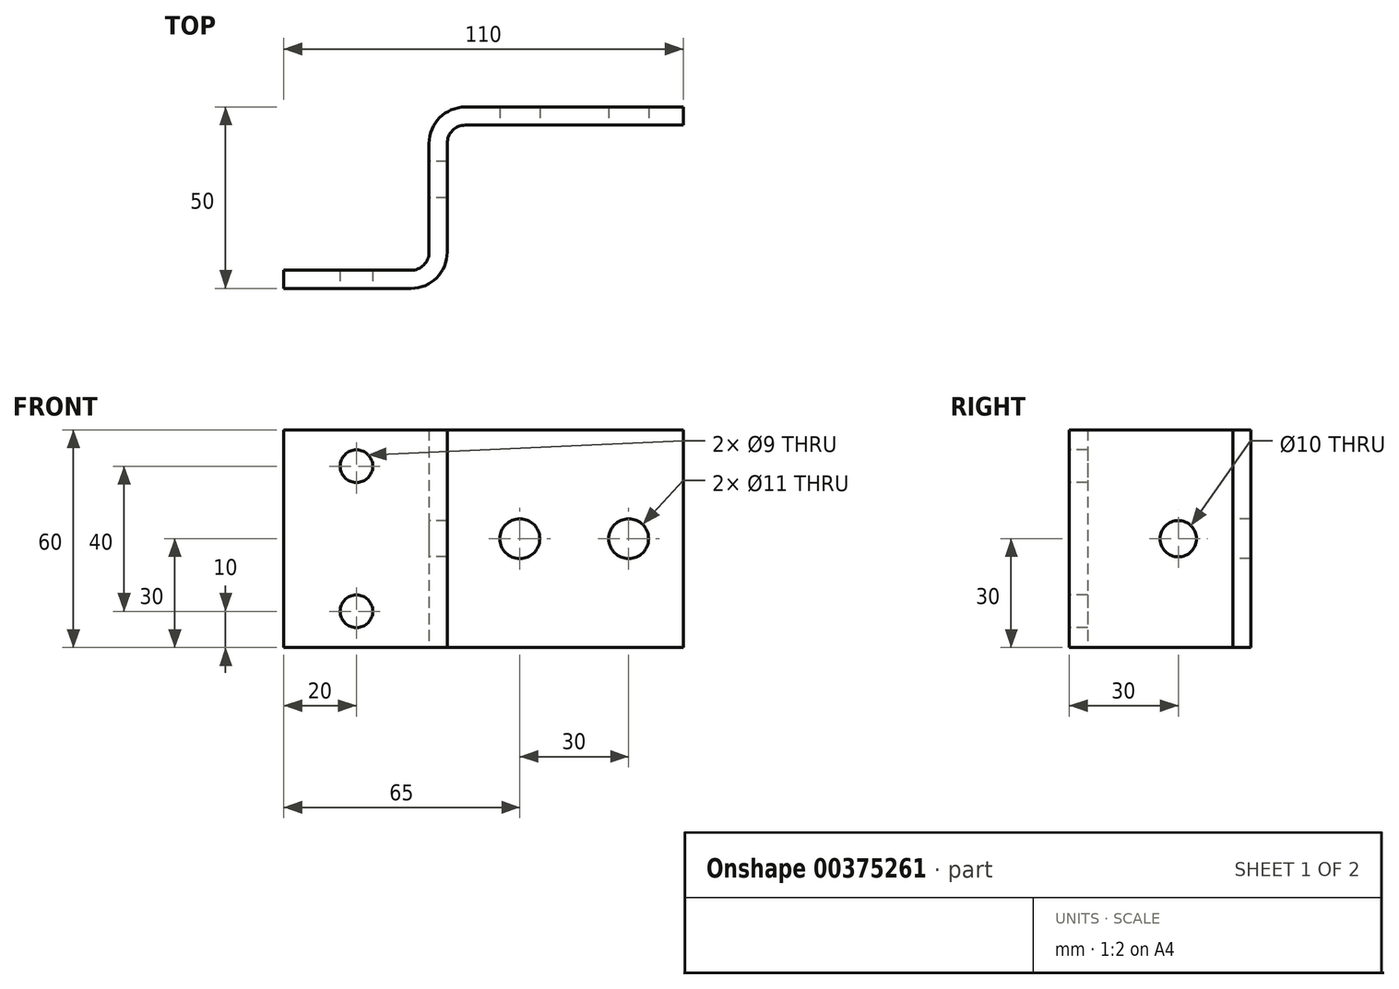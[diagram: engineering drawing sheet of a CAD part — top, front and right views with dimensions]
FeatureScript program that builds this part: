
annotation { "Feature Type Name" : "Feature", "Feature Type Description" : "" }
export const myFeature = defineFeature(function(context is Context, id is Id, definition is map)
    precondition{}
    {
        {
            var Q0;
            Q0=qCreatedBy(makeId("Top.planeOp"),FACE);
            var sketch = newSketch(context, id + "F0", { "sketchPlane" : qUnion([Q0])});
            skLineSegment(sketch, "E0", {"start": v(0, 0) * mm, "end": v(0, 5) * mm});
            skLineSegment(sketch, "E1", {"start": v(0, 5) * mm, "end": v(35, 5) * mm});
            skLineSegment(sketch, "E2", {"start": v(35, 0) * mm, "end": v(0, 0) * mm});
            skLineSegment(sketch, "E3", {"start": v(40, 10) * mm, "end": v(40, 40) * mm});
            skLineSegment(sketch, "E4", {"start": v(50, 50) * mm, "end": v(110, 50) * mm});
            skLineSegment(sketch, "E5", {"start": v(110, 50) * mm, "end": v(110, 45) * mm});
            skLineSegment(sketch, "E6", {"start": v(110, 45) * mm, "end": v(50, 45) * mm});
            skLineSegment(sketch, "E7", {"start": v(45, 40) * mm, "end": v(45, 10) * mm});
            skPoint(sketch, "E8.visualSharp", {"position": v(45, 0) * mm});
            skArc(sketch, "E8.filletArc", {"start": v(35, 0) * mm, "mid": v(42.07, 2.93) * mm, "end": v(45, 10) * mm});
            skPoint(sketch, "E9.orphan", {"position": v(40, 0) * mm});
            skPoint(sketch, "E10.visualSharp", {"position": v(40, 5) * mm});
            skArc(sketch, "E10.filletArc", {"start": v(35, 5) * mm, "mid": v(38.54, 6.46) * mm, "end": v(40, 10) * mm});
            skPoint(sketch, "E11.orphan", {"position": v(40, 45) * mm});
            skPoint(sketch, "E12.visualSharp", {"position": v(45, 45) * mm});
            skArc(sketch, "E12.filletArc", {"start": v(50, 45) * mm, "mid": v(46.46, 43.54) * mm, "end": v(45, 40) * mm});
            skPoint(sketch, "E13.visualSharp", {"position": v(40, 50) * mm});
            skArc(sketch, "E13.filletArc", {"start": v(50, 50) * mm, "mid": v(42.93, 47.07) * mm, "end": v(40, 40) * mm});
            skSolve(sketch);
        }
        {
            var Q0;
            Q0 = qSketchRegion(id + "F0", true);
            extrude(context, id + "F1", {"entities" : qUnion([Q0]), "depth" : 60 * mm});
        }
        {
            var Q0;
            Q0=makeQuery(id+"F1.opExtrude","SWEPT_FACE",FACE,{"disambiguationData":[OSD([sQuery(id+"F0.wireOp",EDGE,"E2")])]});
            var sketch = newSketch(context, id + "F2", { "sketchPlane" : qUnion([Q0])});
            skLineSegment(sketch, "E14", {"start": v(0, 60) * mm, "end": v(20, 60) * mm});
            skLineSegment(sketch, "E15", {"start": v(20, 60) * mm, "end": v(20, 50) * mm});
            skLineSegment(sketch, "E16", {"start": v(20, 50) * mm, "end": v(20, 10) * mm});
            skCircle(sketch, "E17", {"center": v(20, 50) * mm, "radius": 4.5 * mm});
            skCircle(sketch, "E18", {"center": v(20, 10) * mm, "radius": 4.5 * mm});
            skLineSegment(sketch, "E19", {"start": v(20, 60) * mm, "end": v(65, 60) * mm});
            skLineSegment(sketch, "E20", {"start": v(65, 60) * mm, "end": v(95, 60) * mm});
            skLineSegment(sketch, "E21", {"start": v(65, 60) * mm, "end": v(65, 30) * mm});
            skLineSegment(sketch, "E22", {"start": v(65, 30) * mm, "end": v(95, 30) * mm});
            skCircle(sketch, "E23", {"center": v(65, 30) * mm, "radius": 5.5 * mm});
            skCircle(sketch, "E24", {"center": v(95, 30) * mm, "radius": 5.5 * mm});
            skSolve(sketch);
        }
        {
            var Q0;
            Q0 = qSketchRegion(id + "F2", true);
            extrude(context, id + "F3", {"entities" : qUnion([Q0]), "operationType" : NewBodyOperationType.REMOVE, "oppositeDirection" : true, "depth" : 106.9 * mm});
        }
        {
            var Q0;
            Q0=makeQuery(id+"F1.opExtrude","SWEPT_FACE",FACE,{"disambiguationData":[OSD([sQuery(id+"F0.wireOp",EDGE,"E3")])]});
            var sketch = newSketch(context, id + "F4", { "sketchPlane" : qUnion([Q0])});
            skLineSegment(sketch, "E25", {"start": v(-40, 0) * mm, "end": v(-50, 0) * mm});
            skLineSegment(sketch, "E26", {"start": v(-50, 0) * mm, "end": v(-50, 30) * mm});
            skLineSegment(sketch, "E27", {"start": v(-50, 30) * mm, "end": v(-30, 30) * mm});
            skCircle(sketch, "E28", {"center": v(-30, 30) * mm, "radius": 5 * mm});
            skSolve(sketch);
        }
        {
            var Q0;
            Q0 = qSketchRegion(id + "F4", true);
            extrude(context, id + "F5", {"entities" : qUnion([Q0]), "operationType" : NewBodyOperationType.REMOVE, "oppositeDirection" : true, "depth" : 25 * mm});
        }
    });
